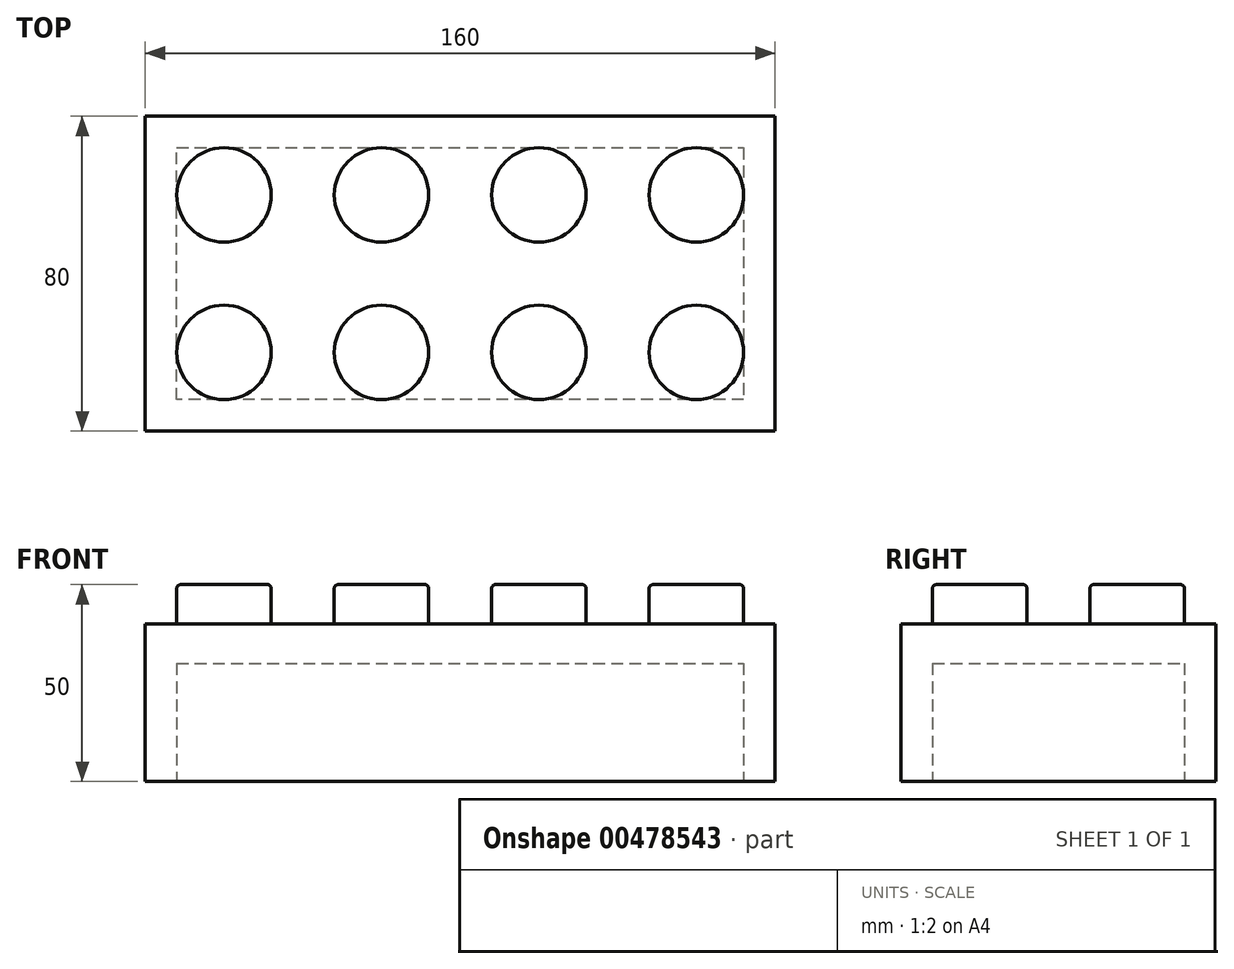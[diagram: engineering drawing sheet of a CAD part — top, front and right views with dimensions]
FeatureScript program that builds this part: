
annotation { "Feature Type Name" : "Feature", "Feature Type Description" : "" }
export const myFeature = defineFeature(function(context is Context, id is Id, definition is map)
    precondition{}
    {
        {
            var Q0;
            Q0=qCreatedBy(makeId("Top.planeOp"),FACE);
            var sketch = newSketch(context, id + "F0", { "sketchPlane" : qUnion([Q0])});
            skLineSegment(sketch, "E0.bottom", {"start": v(-92.86, -36.23) * mm, "end": v(67.14, -36.23) * mm});
            skLineSegment(sketch, "E0.top", {"start": v(-92.86, 43.77) * mm, "end": v(67.14, 43.77) * mm});
            skLineSegment(sketch, "E0.left", {"start": v(-92.86, -36.23) * mm, "end": v(-92.86, 43.77) * mm});
            skLineSegment(sketch, "E0.right", {"start": v(67.14, -36.23) * mm, "end": v(67.14, 43.77) * mm});
            skSolve(sketch);
        }
        {
            var Q0;
            Q0 = qSketchRegion(id + "F0", true);
            extrude(context, id + "F1", {"entities" : qUnion([Q0]), "depth" : 40 * mm});
        }
        {
            var Q0;
            Q0=makeQuery(id+"F1.opExtrude","CAP_FACE",FACE,{"disambiguationData":[OSD([sQuery(id+"F0.wireOp",EDGE,"E0.bottom"),sQuery(id+"F0.wireOp",EDGE,"E0.top"),sQuery(id+"F0.wireOp",EDGE,"E0.left"),sQuery(id+"F0.wireOp",EDGE,"E0.right")])],"isStart":true});
            var sketch = newSketch(context, id + "F2", { "sketchPlane" : qUnion([Q0])});
            skLineSegment(sketch, "E1.0", {"start": v(-84.86, -35.77) * mm, "end": v(59.14, -35.77) * mm});
            skLineSegment(sketch, "E1.1", {"start": v(-84.86, 28.23) * mm, "end": v(-84.86, -35.77) * mm});
            skLineSegment(sketch, "E1.2", {"start": v(59.14, 28.23) * mm, "end": v(-84.86, 28.23) * mm});
            skLineSegment(sketch, "E1.3", {"start": v(59.14, -35.77) * mm, "end": v(59.14, 28.23) * mm});
            skSolve(sketch);
        }
        {
            var Q0;
            Q0 = qSketchRegion(id + "F2", true);
            extrude(context, id + "F3", {"entities" : qUnion([Q0]), "operationType" : NewBodyOperationType.REMOVE, "oppositeDirection" : true, "depth" : 30 * mm});
        }
        {
            var Q0;
            Q0=makeQuery(id+"F1.opExtrude","CAP_FACE",FACE,{"disambiguationData":[OSD([sQuery(id+"F0.wireOp",EDGE,"E0.bottom"),sQuery(id+"F0.wireOp",EDGE,"E0.top"),sQuery(id+"F0.wireOp",EDGE,"E0.left"),sQuery(id+"F0.wireOp",EDGE,"E0.right")])],"isStart":false});
            var sketch = newSketch(context, id + "F4", { "sketchPlane" : qUnion([Q0])});
            skCircle(sketch, "E2", {"center": v(-72.86, 23.77) * mm, "radius": 12 * mm});
            skCircle(sketch, "E3.0.1.0", {"center": v(-72.86, -16.23) * mm, "radius": 12 * mm});
            skCircle(sketch, "E3.1.0.0", {"center": v(-32.86, 23.77) * mm, "radius": 12 * mm});
            skCircle(sketch, "E3.1.1.0", {"center": v(-32.86, -16.23) * mm, "radius": 12 * mm});
            skCircle(sketch, "E3.2.0.0", {"center": v(7.14, 23.77) * mm, "radius": 12 * mm});
            skCircle(sketch, "E3.2.1.0", {"center": v(7.14, -16.23) * mm, "radius": 12 * mm});
            skCircle(sketch, "E3.3.0.0", {"center": v(47.14, 23.77) * mm, "radius": 12 * mm});
            skCircle(sketch, "E3.3.1.0", {"center": v(47.14, -16.23) * mm, "radius": 12 * mm});
            skLineSegment(sketch, "E3.direction1", {"start": v(-72.86, 23.77) * mm, "end": v(-32.86, 23.77) * mm, "construction": true});
            skLineSegment(sketch, "E3.direction2", {"start": v(-72.86, 23.77) * mm, "end": v(-72.86, -16.23) * mm, "construction": true});
            skSolve(sketch);
        }
        {
            var Q0;
            Q0 = qSketchRegion(id + "F4", true);
            var Q1;
            Q1 = qConstructionFilter(qBodyType(qCreatedBy(id + "F4" ,EDGE), BodyType.WIRE), ConstructionObject.NO);
            extrude(context, id + "F5", {"entities" : qUnion([Q0]), "operationType" : NewBodyOperationType.ADD, "surfaceEntities" : qUnion([Q1]), "depth" : 10 * mm});
        }
        {
            var Q0;
            Q0=makeQuery(id+"F5.opExtrude","CAP_FACE",FACE,{"disambiguationData":[OSD([sQuery(id+"F4.wireOp",EDGE,"E2")])],"isStart":false});
            var Q1;
            Q1=makeQuery(id+"F5.opExtrude","CAP_FACE",FACE,{"disambiguationData":[OSD([sQuery(id+"F4.wireOp",EDGE,"E3.1.1.0")])],"isStart":false});
            var Q2;
            Q2=makeQuery(id+"F5.opExtrude","CAP_FACE",FACE,{"disambiguationData":[OSD([sQuery(id+"F4.wireOp",EDGE,"E3.1.0.0")])],"isStart":false});
            var Q3;
            Q3=makeQuery(id+"F5.opExtrude","CAP_FACE",FACE,{"disambiguationData":[OSD([sQuery(id+"F4.wireOp",EDGE,"E3.0.1.0")])],"isStart":false});
            var Q4;
            Q4=makeQuery(id+"F5.opExtrude","CAP_FACE",FACE,{"disambiguationData":[OSD([sQuery(id+"F4.wireOp",EDGE,"E3.2.1.0")])],"isStart":false});
            var Q5;
            Q5=makeQuery(id+"F5.opExtrude","CAP_FACE",FACE,{"disambiguationData":[OSD([sQuery(id+"F4.wireOp",EDGE,"E3.2.0.0")])],"isStart":false});
            var Q6;
            Q6=makeQuery(id+"F5.opExtrude","CAP_FACE",FACE,{"disambiguationData":[OSD([sQuery(id+"F4.wireOp",EDGE,"E3.3.1.0")])],"isStart":false});
            var Q7;
            Q7=makeQuery(id+"F5.opExtrude","CAP_FACE",FACE,{"disambiguationData":[OSD([sQuery(id+"F4.wireOp",EDGE,"E3.3.0.0")])],"isStart":false});
            fillet(context, id + "F6", {"entities" : qUnion([Q0, Q1, Q2, Q3, Q4, Q5, Q6, Q7]), "radius" : 1 * mm, "tangentPropagation" : true, "allowEdgeOverflow" : false});
        }
    });
